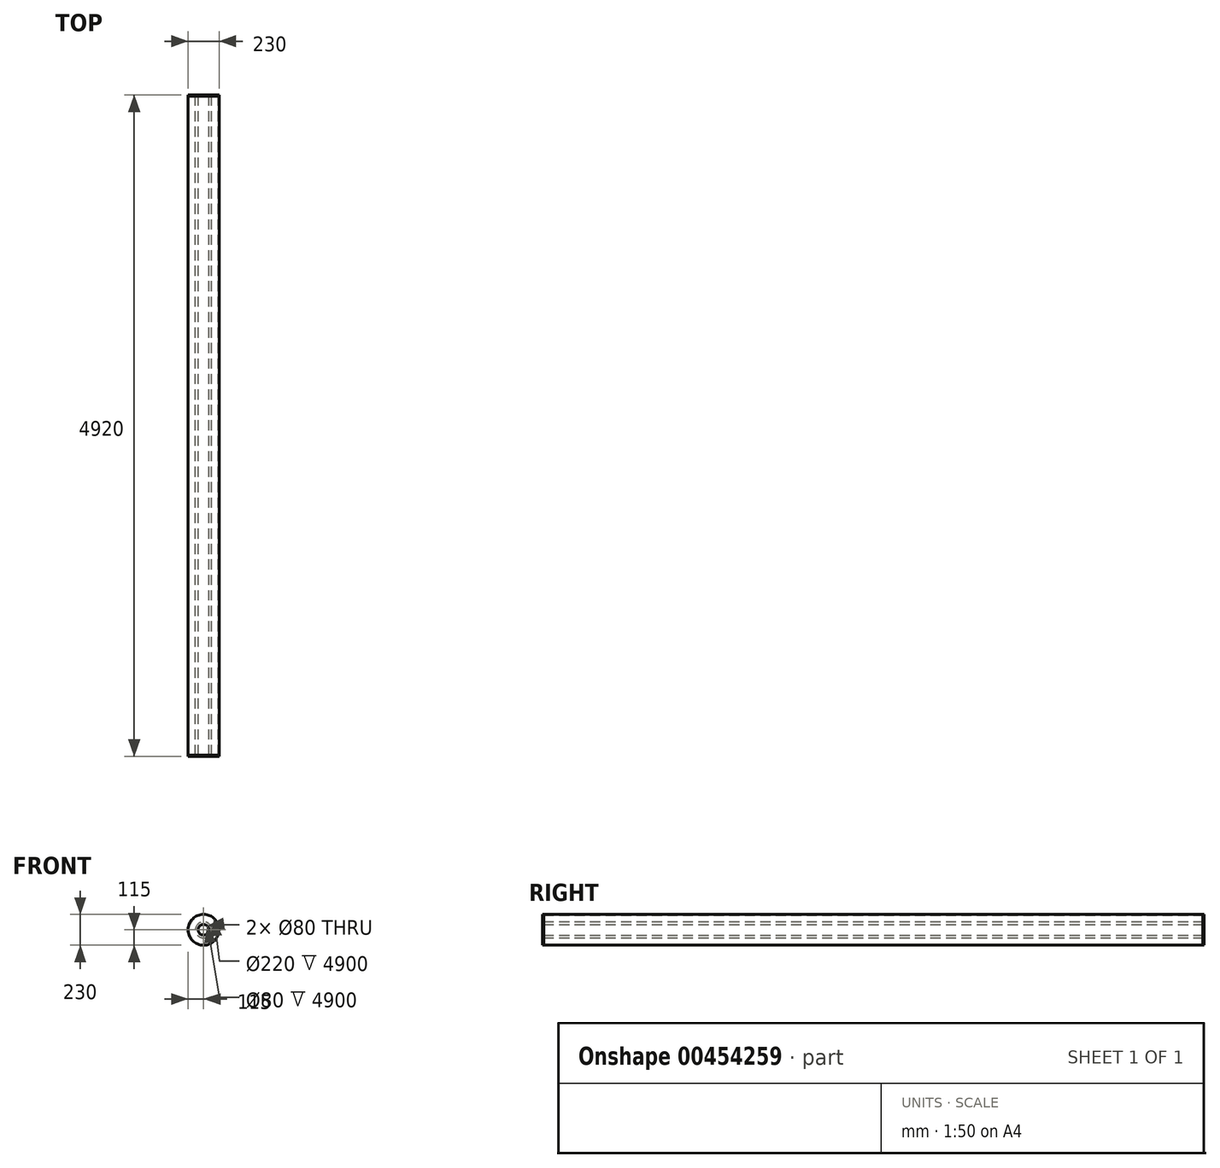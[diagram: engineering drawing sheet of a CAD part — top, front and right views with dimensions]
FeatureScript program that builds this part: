
annotation { "Feature Type Name" : "Feature", "Feature Type Description" : "" }
export const myFeature = defineFeature(function(context is Context, id is Id, definition is map)
    precondition{}
    {
        {
            var Q0;
            Q0=qCreatedBy(makeId("Front.planeOp"),FACE);
            var sketch = newSketch(context, id + "F0", { "sketchPlane" : qUnion([Q0])});
            skCircle(sketch, "E0", {"center": v(0, 0) * mm, "radius": 40 * mm});
            skCircle(sketch, "E1", {"center": v(0, 0) * mm, "radius": 60 * mm});
            skCircle(sketch, "E2", {"center": v(0, 0) * mm, "radius": 110 * mm});
            skCircle(sketch, "E3", {"center": v(0, 0) * mm, "radius": 115 * mm});
            skSolve(sketch);
        }
        {
            var Q0;
            Q0=makeQuery(id+"F0.imprint","IMPRINT",FACE,{"disambiguationData":[TD([[makeQuery(id+"F0.imprint","IMPRINT",EDGE,{"derivedFrom":sQuery(id+"F0.wireOp",EDGE,"E0")}),-1.0]])]});
            var Q1;
            Q1=makeQuery(id+"F0.imprint","IMPRINT",FACE,{"disambiguationData":[TD([[makeQuery(id+"F0.imprint","IMPRINT",EDGE,{"derivedFrom":sQuery(id+"F0.wireOp",EDGE,"E2")}),-1.0]])]});
            extrude(context, id + "F1", {"entities" : qUnion([Q0, Q1]), "depth" : 4900 * mm});
        }
        {
            var Q0;
            Q0=makeQuery(id+"F1.opExtrude","CAP_FACE",FACE,{"disambiguationData":[OSD([sQuery(id+"F0.wireOp",EDGE,"E0"),sQuery(id+"F0.wireOp",EDGE,"E1")])],"isStart":false});
            var sketch = newSketch(context, id + "F2", { "sketchPlane" : qUnion([Q0])});
            skCircle(sketch, "E4.0", {"center": v(0, 0) * mm, "radius": 115 * mm});
            skCircle(sketch, "E5.0", {"center": v(0, 0) * mm, "radius": 40 * mm});
            skSolve(sketch);
        }
        {
            var Q0;
            Q0 = qSketchRegion(id + "F2", true);
            extrude(context, id + "F3", {"entities" : qUnion([Q0]), "depth" : 10 * mm});
        }
        {
            var Q0;
            Q0=makeQuery(id+"F1.opExtrude","CAP_FACE",FACE,{"disambiguationData":[OSD([sQuery(id+"F0.wireOp",EDGE,"E0"),sQuery(id+"F0.wireOp",EDGE,"E1")])],"isStart":true});
            var sketch = newSketch(context, id + "F4", { "sketchPlane" : qUnion([Q0])});
            skCircle(sketch, "E6.0", {"center": v(0, 0) * mm, "radius": 115 * mm});
            skCircle(sketch, "E7.0", {"center": v(0, 0) * mm, "radius": 40 * mm});
            skSolve(sketch);
        }
        {
            var Q0;
            Q0 = qSketchRegion(id + "F4", true);
            extrude(context, id + "F5", {"entities" : qUnion([Q0]), "depth" : 10 * mm});
        }
    });
